# Revit family: Sanitary_Dispensers_Svedholm_Slits-top-loaded-paper-dispenser
name_source: partatom
category: Furniture
revit_build: Autodesk Revit 2018 (Build: 20170223_1515(x64)
units: mm (PartAtom-declared; Revit-internal decimal feet)

## family parameters
Cut with Voids When Loaded = No
Host = Face
OmniClass Number = 23.21.11.00
OmniClass Title = Commercial Furniture
Room Calculation Point = No
Shared = No

## types (1)
- ART - (410.600.001)
    BIMobject category = Dispensers
    Default Elevation = 1219 mm
    Description = Paper Dispenser made of powder coated steel. Adapted for paper towels 240 x 95 mm. Tork Soft C-fold H3 or equivalent.
    Edition number = 1
    IFC Classification = Object
    Manufacturer = Svedholm
    Manufacturer name = Svedholm
    Model = Slits top loaded paper dispenser
    OmniClass Code = 23-21 11 00
    OmniClass Description = Commercial Furniture
    Product Guid = 0d045c15-3881-47ac-8e00-ffb4c80614ab
    Product SKU = slits-top-loaded-paper-dispenser
    Product data url = https://bimobject.com
    Product family = Slits
    Product group = Dispenser
    Product name = Slits top loaded paper dispenser
    Product url = https://www.svedholm.se
    QR code = https://bimobject.com
    URL = https://www.svedholm.se
    Uniclass 2015 Code = Zz_30_60
    Uniclass 2015 Name = Objects

## geometry (parser evidence)
native form markers: Sweep x3
no freeform markers — native parametric forms only
